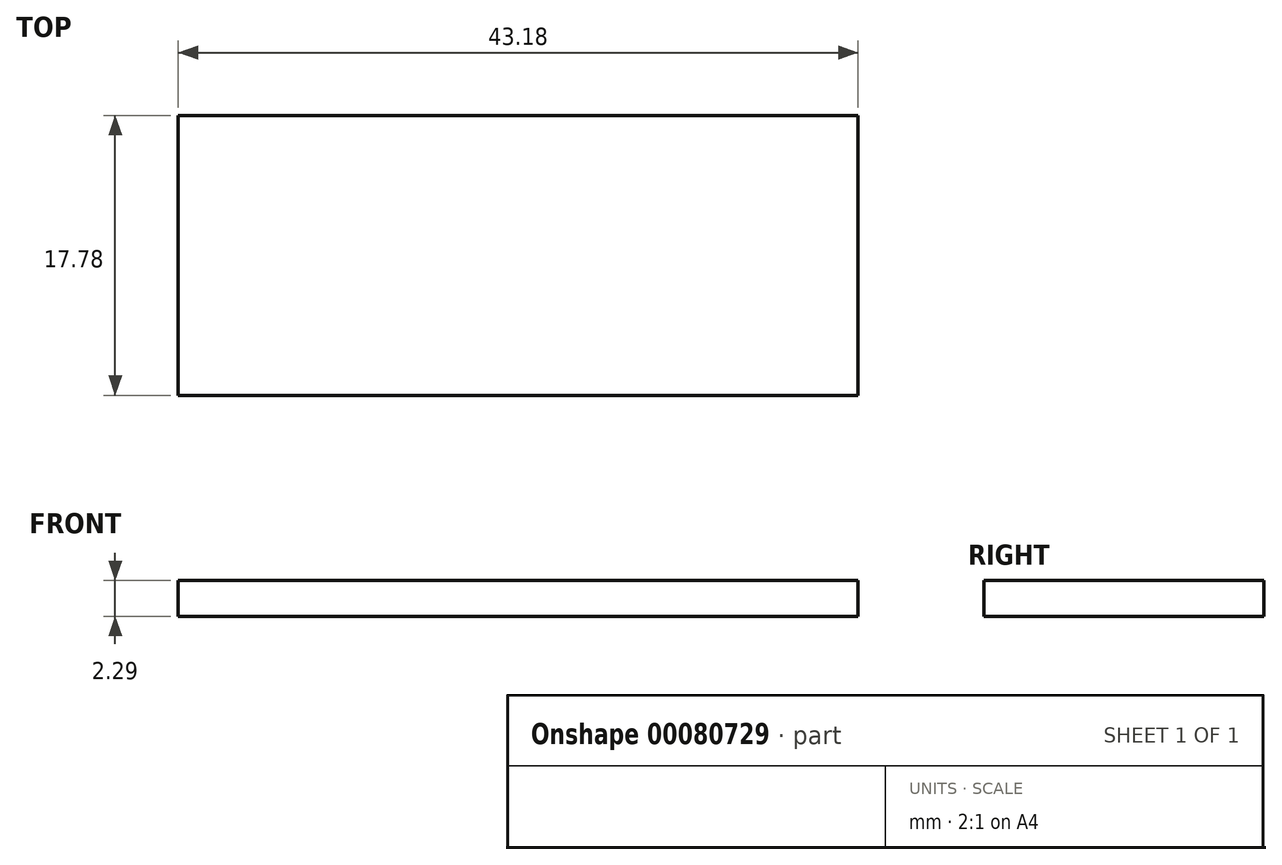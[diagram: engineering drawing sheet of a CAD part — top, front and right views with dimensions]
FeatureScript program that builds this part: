
annotation { "Feature Type Name" : "Feature", "Feature Type Description" : "" }
export const myFeature = defineFeature(function(context is Context, id is Id, definition is map)
    precondition{}
    {
        {
            var Q0;
            Q0=qCreatedBy(makeId("Top.planeOp"),FACE);
            var sketch = newSketch(context, id + "F0", { "sketchPlane" : qUnion([Q0])});
            skLineSegment(sketch, "E0.bottom", {"start": v(21.59, -8.89) * mm, "end": v(-21.59, -8.9) * mm});
            skLineSegment(sketch, "E0.top", {"start": v(21.59, 8.9) * mm, "end": v(-21.59, 8.89) * mm});
            skLineSegment(sketch, "E0.left", {"start": v(21.59, -8.89) * mm, "end": v(21.59, 8.9) * mm});
            skLineSegment(sketch, "E0.right", {"start": v(-21.59, -8.9) * mm, "end": v(-21.6, 8.89) * mm});
            skPoint(sketch, "E0.middle", {"position": v(0, 0) * mm});
            skSolve(sketch);
        }
        {
            var Q0;
            Q0=makeQuery(id+"F0.imprint","IMPRINT",FACE,{"disambiguationData":[TD([[makeQuery(id+"F0.imprint","IMPRINT",EDGE,{"derivedFrom":sQuery(id+"F0.wireOp",EDGE,"E0.bottom")}),-1.0]])]});
            extrude(context, id + "F1", {"entities" : qUnion([Q0]), "depth" : 2.3 * mm});
        }
    });
